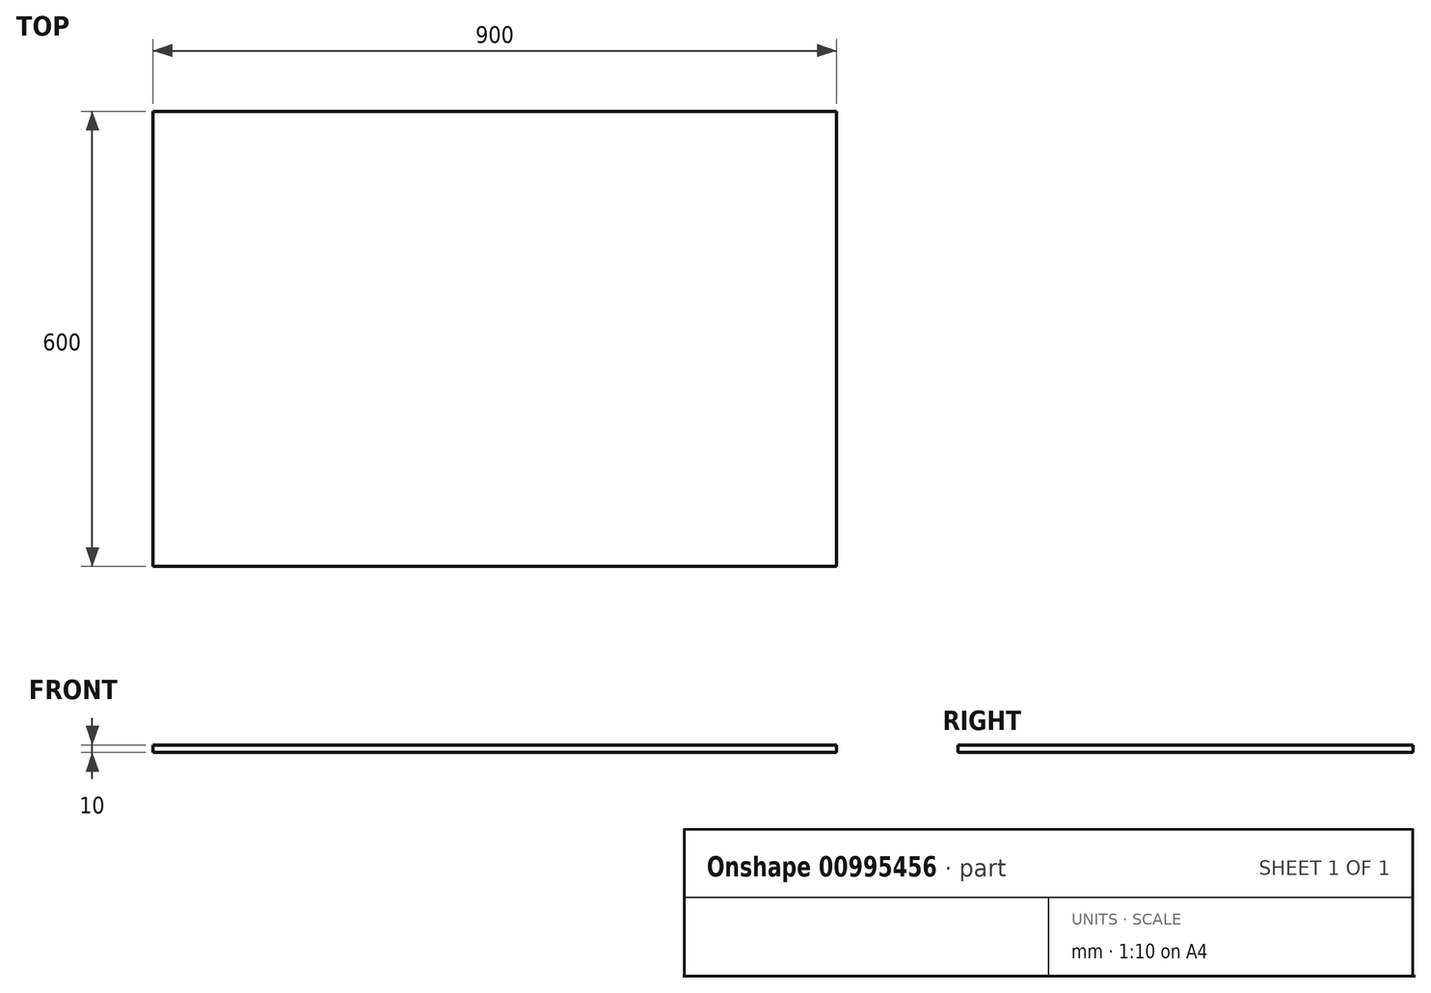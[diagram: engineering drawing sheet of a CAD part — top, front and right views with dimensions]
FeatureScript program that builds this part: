
annotation { "Feature Type Name" : "Feature", "Feature Type Description" : "" }
export const myFeature = defineFeature(function(context is Context, id is Id, definition is map)
    precondition{}
    {
        {
            var Q0;
            Q0=qCreatedBy(makeId("Top.planeOp"),FACE);
            var sketch = newSketch(context, id + "F0", { "sketchPlane" : qUnion([Q0])});
            skLineSegment(sketch, "E0.bottom", {"start": v(450, -300) * mm, "end": v(-450, -300) * mm});
            skLineSegment(sketch, "E0.top", {"start": v(450, 300) * mm, "end": v(-450, 300) * mm});
            skLineSegment(sketch, "E0.left", {"start": v(450, -300) * mm, "end": v(450, 300) * mm});
            skLineSegment(sketch, "E0.right", {"start": v(-450, -300) * mm, "end": v(-450, 300) * mm});
            skPoint(sketch, "E0.middle", {"position": v(0, 0) * mm});
            skSolve(sketch);
        }
        {
            var Q0;
            Q0 = qSketchRegion(id + "F0", true);
            extrude(context, id + "F1", {"entities" : qUnion([Q0]), "depth" : 10 * mm, "offsetDistance" : 25 * mm});
        }
    });
